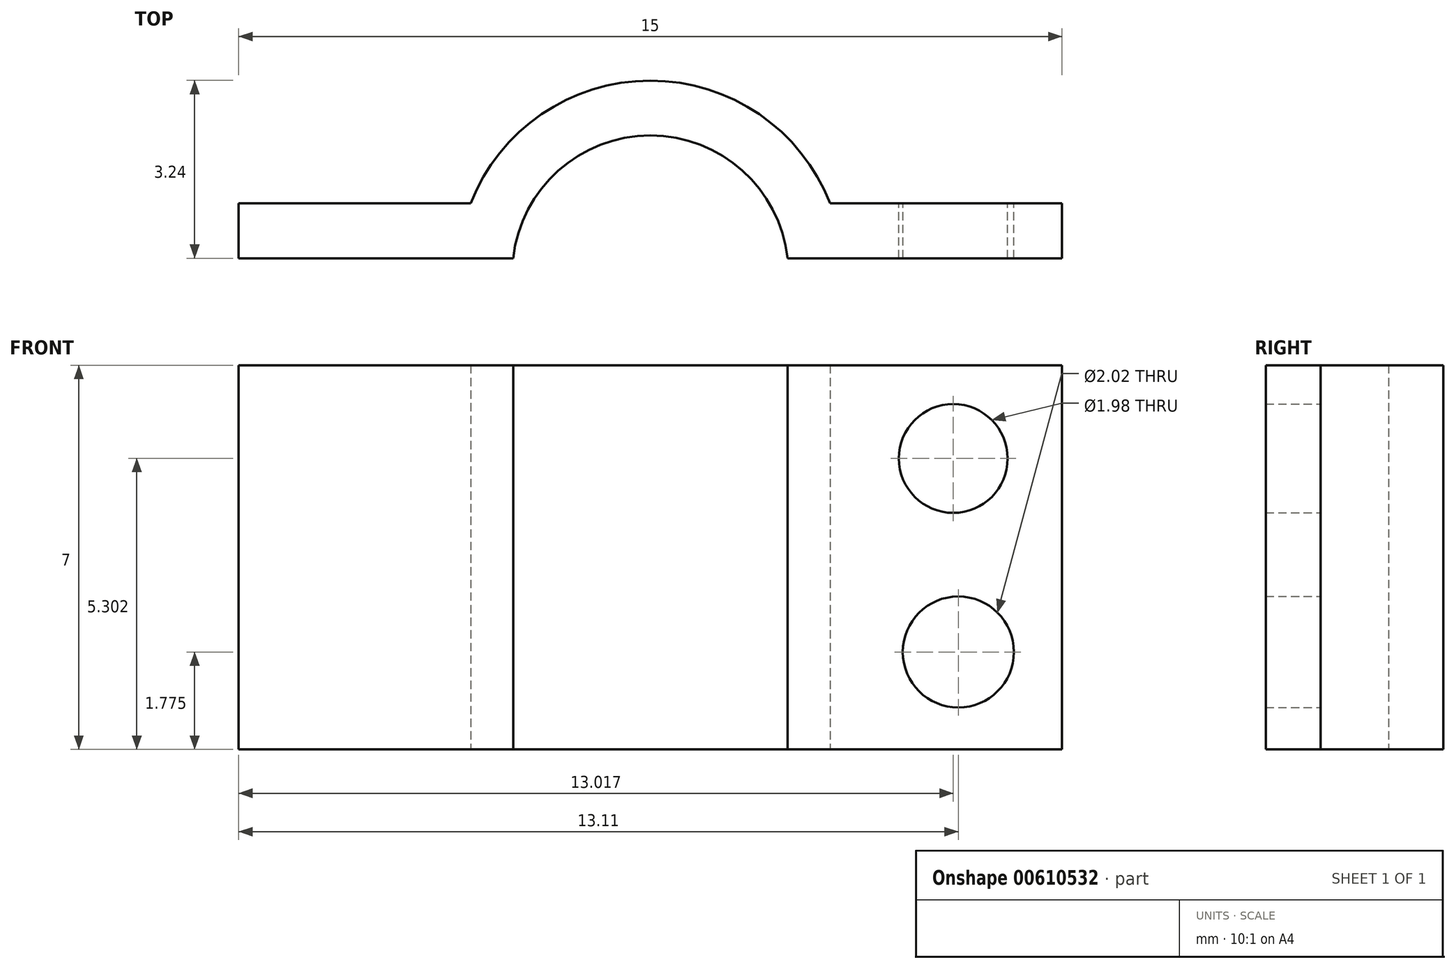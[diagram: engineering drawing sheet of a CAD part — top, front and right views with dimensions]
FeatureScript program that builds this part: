
annotation { "Feature Type Name" : "Feature", "Feature Type Description" : "" }
export const myFeature = defineFeature(function(context is Context, id is Id, definition is map)
    precondition{}
    {
        {
            var Q0;
            Q0=qCreatedBy(makeId("Top.planeOp"),FACE);
            var sketch = newSketch(context, id + "F0", { "sketchPlane" : qUnion([Q0])});
            skLineSegment(sketch, "E0", {"start": v(0, 0) * mm, "end": v(5, 0) * mm});
            skLineSegment(sketch, "E1", {"start": v(5, 0) * mm, "end": v(10, 0) * mm});
            skLineSegment(sketch, "E2", {"start": v(10, 0) * mm, "end": v(15, 0) * mm});
            skArc(sketch, "E3", {"start": v(10, 0) * mm, "mid": v(7.5, 2.24) * mm, "end": v(5, 0) * mm});
            skLineSegment(sketch, "E4.0", {"start": v(10.77, 1) * mm, "end": v(15, 1) * mm});
            skArc(sketch, "E4.1", {"start": v(10.77, 1) * mm, "mid": v(7.5, 3.24) * mm, "end": v(4.23, 1) * mm});
            skLineSegment(sketch, "E4.2", {"start": v(0, 1) * mm, "end": v(4.23, 1) * mm});
            skLineSegment(sketch, "E5", {"start": v(0, 1) * mm, "end": v(0, 0) * mm});
            skLineSegment(sketch, "E6", {"start": v(15, 1) * mm, "end": v(15, 0) * mm});
            skSolve(sketch);
        }
        {
            var Q0;
            Q0=makeQuery(id+"F0.imprint","IMPRINT",FACE,{"disambiguationData":[TD([[makeQuery(id+"F0.imprint","IMPRINT",EDGE,{"derivedFrom":sQuery(id+"F0.wireOp",EDGE,"E0")}),1.0]])]});
            extrude(context, id + "F1", {"entities" : qUnion([Q0]), "depth" : 7 * mm, "offsetDistance" : 25 * mm});
        }
        {
            var Q0;
            Q0=makeQuery(id+"F1.opExtrude","SWEPT_FACE",FACE,{"disambiguationData":[OSD([sQuery(id+"F0.wireOp",EDGE,"E4.0")])]});
            var sketch = newSketch(context, id + "F2", { "sketchPlane" : qUnion([Q0])});
            skCircle(sketch, "E7", {"center": v(-13.02, 5.3) * mm, "radius": 1 * mm});
            skCircle(sketch, "E8", {"center": v(-13.11, 1.77) * mm, "radius": 1.01 * mm});
            skLineSegment(sketch, "E9", {"start": v(-10.77, 7) * mm, "end": v(-4.2, 7) * mm});
            skLineSegment(sketch, "E10", {"start": v(-7.5, 7) * mm, "end": v(-7.5, -1.16) * mm});
            skCircle(sketch, "E11.MirrorC", {"center": v(-1.96, 5.3) * mm, "radius": 1 * mm});
            skCircle(sketch, "E12.MirrorC", {"center": v(-1.87, 1.77) * mm, "radius": 1.01 * mm});
            skSolve(sketch);
        }
        {
            var Q0;
            Q0=makeQuery(id+"F2.imprint","IMPRINT",FACE,{"disambiguationData":[TD([[makeQuery(id+"F2.imprint","IMPRINT",EDGE,{"derivedFrom":sQuery(id+"F2.wireOp",EDGE,"E7")}),1.0]])]});
            var Q1;
            Q1=makeQuery(id+"F2.imprint","IMPRINT",FACE,{"disambiguationData":[TD([[makeQuery(id+"F2.imprint","IMPRINT",EDGE,{"derivedFrom":sQuery(id+"F2.wireOp",EDGE,"E8")}),1.0]])]});
            var Q2;
            Q2=makeQuery(id+"F2.imprint","IMPRINT",FACE,{"disambiguationData":[TD([[makeQuery(id+"F2.imprint","IMPRINT",EDGE,{"derivedFrom":sQuery(id+"F2.wireOp",EDGE,"E12.MirrorC")}),-1.0]])]});
            var Q3;
            Q3=makeQuery(id+"F2.imprint","IMPRINT",FACE,{"disambiguationData":[TD([[makeQuery(id+"F2.imprint","IMPRINT",EDGE,{"derivedFrom":sQuery(id+"F2.wireOp",EDGE,"E11.MirrorC")}),-1.0]])]});
            extrude(context, id + "F3", {"entities" : qUnion([Q0, Q1, Q2, Q3]), "operationType" : NewBodyOperationType.REMOVE, "oppositeDirection" : true, "depth" : 25 * mm, "offsetDistance" : 25 * mm});
        }
    });
